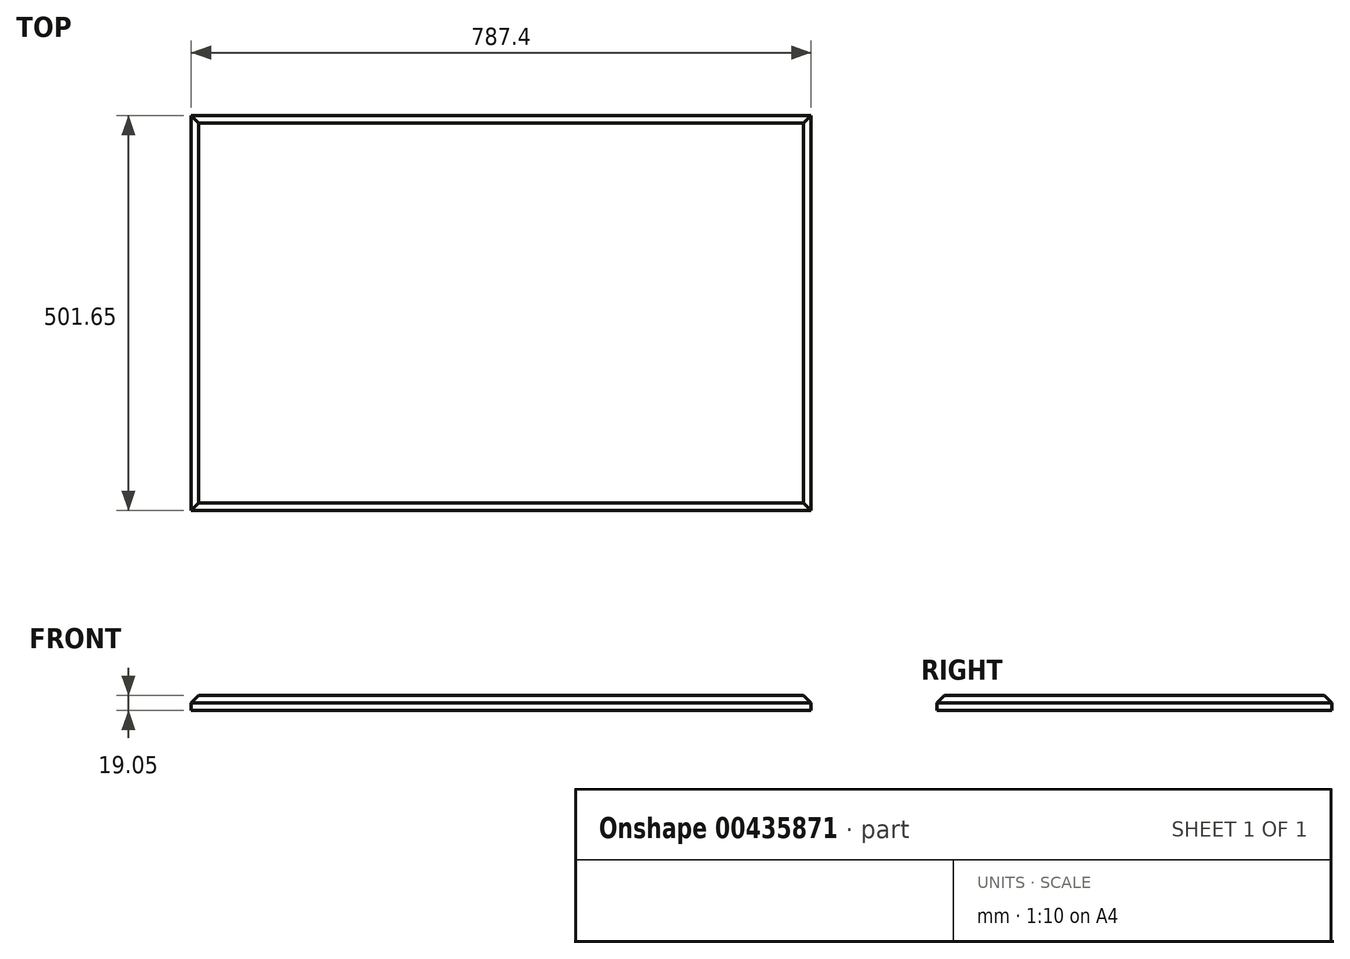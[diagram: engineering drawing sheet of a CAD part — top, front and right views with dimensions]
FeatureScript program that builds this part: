
annotation { "Feature Type Name" : "Feature", "Feature Type Description" : "" }
export const myFeature = defineFeature(function(context is Context, id is Id, definition is map)
    precondition{}
    {
        {
            var Q0;
            Q0=qCreatedBy(makeId("Top.planeOp"),FACE);
            var sketch = newSketch(context, id + "F0", { "sketchPlane" : qUnion([Q0])});
            skLineSegment(sketch, "E0.bottom", {"start": v(0, 0) * mm, "end": v(787.4, 0) * mm});
            skLineSegment(sketch, "E0.top", {"start": v(0, 501.65) * mm, "end": v(787.4, 501.65) * mm});
            skLineSegment(sketch, "E0.left", {"start": v(0, 0) * mm, "end": v(0, 501.65) * mm});
            skLineSegment(sketch, "E0.right", {"start": v(787.4, 0) * mm, "end": v(787.4, 501.65) * mm});
            skSolve(sketch);
        }
        {
            var Q0;
            Q0=makeQuery(id+"F0.imprint","IMPRINT",FACE,{"disambiguationData":[TD([[makeQuery(id+"F0.imprint","IMPRINT",EDGE,{"derivedFrom":sQuery(id+"F0.wireOp",EDGE,"E0.bottom")}),1.0]])]});
            extrude(context, id + "F1", {"entities" : qUnion([Q0]), "depth" : 19.05 * mm});
        }
        {
            var Q0;
            Q0=makeQuery(id+"F1.opExtrude","CAP_EDGE",EDGE,{"disambiguationData":[OSD([sQuery(id+"F0.wireOp",EDGE,"E0.left")])],"isStart":false});
            var Q1;
            Q1=makeQuery(id+"F1.opExtrude","CAP_EDGE",EDGE,{"disambiguationData":[OSD([sQuery(id+"F0.wireOp",EDGE,"E0.bottom")])],"isStart":false});
            var Q2;
            Q2=makeQuery(id+"F1.opExtrude","CAP_EDGE",EDGE,{"disambiguationData":[OSD([sQuery(id+"F0.wireOp",EDGE,"E0.right")])],"isStart":false});
            var Q3;
            Q3=makeQuery(id+"F1.opExtrude","CAP_EDGE",EDGE,{"disambiguationData":[OSD([sQuery(id+"F0.wireOp",EDGE,"E0.top")])],"isStart":false});
            chamfer(context, id + "F2", {"entities" : qUnion([Q0, Q1, Q2, Q3]), "width" : 9.52 * mm, "tangentPropagation" : true});
        }
    });
